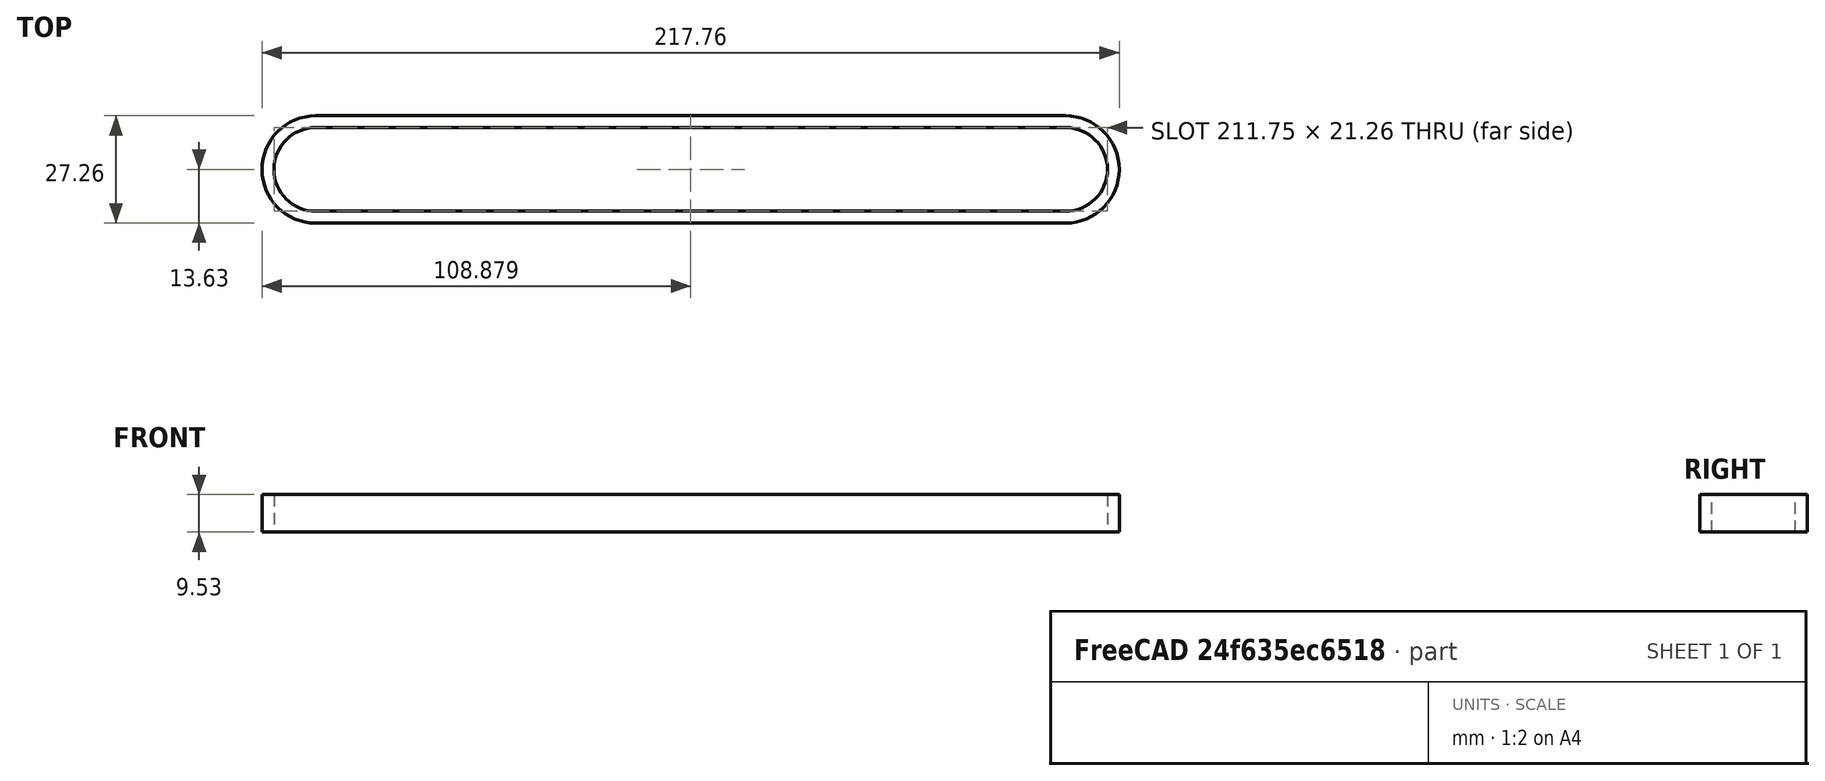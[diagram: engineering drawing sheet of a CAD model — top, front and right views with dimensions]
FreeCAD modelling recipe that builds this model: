
FCSTD DOCUMENT  (FreeCAD 0.19R24276 (Git))
Label: BELT-XL-180-375
License: All rights reserved
LicenseURL: http://en.wikipedia.org/wiki/All_rights_reserved
objects: Sketcher::SketchObject×1, PartDesign::Pad×1, PartDesign::CoordinateSystem×1, PartDesign::Body×1
note: 5 computed .brp shape members not serialized (recipe doc carries the construction recipe); baked Part::Feature solids carry a one-line shape summary decoded from their .brp

FEATURE [Sketcher::SketchObject] Sketch
  FullyConstrained = false
  MapMode = 5
  Support = -> [XY_Plane]
  expr: Constraints[7] = 25.4 * 0.955
  expr: Constraints[8] = (18 * 25.4 - 0.955 * 25.4 * pi) / 2
  sketch-geometry (12):
    g0: ArcOfCircle CenterX=0 CenterY=0 CenterZ=0 NormalX=0 NormalY=0 NormalZ=1 AngleXU=0 Radius=12.1285 StartAngle=1.5708 EndAngle=4.71239
    g1: ArcOfCircle CenterX=190.497 CenterY=-6e-16 CenterZ=0 NormalX=0 NormalY=0 NormalZ=1 AngleXU=0 Radius=12.1285 StartAngle=4.71239 EndAngle=7.85398
    g2: LineSegment StartX=0 StartY=-12.1285 StartZ=0 EndX=190.497 EndY=-12.1285 EndZ=0
    g3: LineSegment StartX=-3.9565e-12 StartY=12.1285 StartZ=0 EndX=190.497 EndY=12.1285 EndZ=0
    g4: ArcOfCircle CenterX=0 CenterY=0 CenterZ=0 NormalX=0 NormalY=0 NormalZ=1 AngleXU=0 Radius=10.6285 StartAngle=1.5708 EndAngle=4.71239
    g5: ArcOfCircle CenterX=190.497 CenterY=-6e-16 CenterZ=0 NormalX=0 NormalY=0 NormalZ=1 AngleXU=0 Radius=10.6285 StartAngle=4.71239 EndAngle=7.85398
    g6: LineSegment StartX=0 StartY=-10.6285 StartZ=0 EndX=190.497 EndY=-10.6285 EndZ=0
    g7: LineSegment StartX=-1.3e-15 StartY=10.6285 StartZ=0 EndX=190.497 EndY=10.6285 EndZ=0
    g8: ArcOfCircle CenterX=0 CenterY=0 CenterZ=0 NormalX=0 NormalY=0 NormalZ=1 AngleXU=0 Radius=13.6285 StartAngle=1.5708 EndAngle=4.71239
    g9: ArcOfCircle CenterX=190.497 CenterY=-6e-16 CenterZ=0 NormalX=0 NormalY=0 NormalZ=1 AngleXU=0 Radius=13.6285 StartAngle=4.71239 EndAngle=7.85398
    g10: LineSegment StartX=0 StartY=-13.6285 StartZ=0 EndX=190.497 EndY=-13.6285 EndZ=0
    g11: LineSegment StartX=-1.7e-15 StartY=13.6285 StartZ=0 EndX=190.497 EndY=13.6285 EndZ=0
  constraints (25):
    c: Tangent(g0,g3)
    c: Tangent(g0,g2)
    c: Tangent(g2,g1)
    c: Tangent(g3,g1)
    c: Horizontal(g2)
    c: Equal(g0,g1)
    c: Coincident(g0,g-1)
    c: Diameter(g0) = 24.257
    c: DistanceX(g3,g3) = 190.497
    c: Tangent(g4,g7)
    c: Tangent(g4,g6)
    c: Tangent(g6,g5)
    c: Tangent(g7,g5)
    c: Horizontal(g6)
    c: Coincident(g4,g-1)
    c: Coincident(g1,g5)
    c: Tangent(g8,g11)
    c: Tangent(g8,g10)
    c: Tangent(g10,g9)
    c: Tangent(g11,g9)
    c: Horizontal(g10)
    c: Coincident(g8,g4)
    c: Coincident(g9,g5)
    c: DistanceY(g5,g1) = 1.5
    c: DistanceY(g1,g9) = 1.5
FEATURE [PartDesign::Pad] Pad
  Direction = (1,1,1)
  Length = 9.525
  Length2 = 100
  Profile = -> Sketch
  Type = 0
FEATURE [PartDesign::CoordinateSystem] LCS_1
  AttacherType = Attacher::AttachEngine3D
  MapMode = 11
  Placement = pos=(0,0,0) rot=(0,0,1;3.14159rad)
  Support = -> [Pad]
FEATURE [PartDesign::Body] Body  label="BELT-XL-130-375"
  Group = -> [Sketch,Pad,LCS_1]
  Origin = -> Origin
  Tip = -> Pad
